# Revit family: Valve-Pressure_Relief-Cla_Val-55L_60-FNPT-SI--
name_source: partatom
category: Pipe Accessories
units: mm (PartAtom-declared; Revit-internal decimal feet)

## family parameters
Always vertical = Yes
Cut with Voids When Loaded = No
OmniClass Number = 23.65.55.00
OmniClass Title = Distribution of Supplied Liquids/Gases
Part Type = Valve - Breaks Into
Round Connector Dimension = Use Radius
Shared = No
Work Plane-Based = No

## types (1)
- ERROR_LOAD TYPE CATALOG
    Assembly Code = D2090900
    Bottom Plug Material = Metal - Cla-Val - Stainless Steel
    CV (liters per second) = 0.38
    Cap Height = 57 mm
    Cap Material = Plastic - Cla-Val - Red
    Cap Mount Height = 4 mm
    Cap Mount Radius = 11 mm
    Cap Radius = 10 mm
    Connection Axis to Lower Flange = 33 mm
    Connection Axis to Valve Bottom = 33 mm
    Connection Axis to Valve Top = 171 mm
    Connection Radius = 8 mm
    Connection Size = 15 mm
    Connection Type = Female Thread
    Connection to Connection = 62 mm
    Cover Bevel Radius = 6 mm
    Cover Radius = 17 mm
    Default Elevation = 0 mm
    Description = Pressure Relief Valve
    ENGworks Global = http://www.ENGworksGlobal.com
    Flow Configuration = In/Out
    K Coefficient = 3.717034
    K Coefficient Table = Globe Valve Threaded
    Lock Nut Circumscribe Length = 23 mm
    Lock Nut Height = 15 mm
    Loss Method = K Coefficient
    Lower Flange Height = 6 mm
    Manufacturer = Cla_Val
    Maximum Flow Rate = 1.6 L/s
    Maximum Flow Rate Value = 1.58
    Maximum Operating Temperature = 82 °C
    Maximum Working Pressure = 28 bar
    Minimum Flow Rate = 0.0 L/s
    Minimum Flow Rate Value = 0
    Minimum Operating Temperature = -18 °C
    Model = 55L-60
    Nut Union Circumscribe Length = 31 mm
    Overall Height = 219 mm
    Plug Mount Radius = 13 mm
    Pressure Gauge Port Outside Diameter = 10 mm
    Pressure Gauge Port Outside Radius = 5 mm
    Product Page URL = https://www.cla-val.com
    Series = Pressure Relief Valves
    Standards = UL Listed and FM Approved
    Threaded Female End Insertion Depth = 14 mm
    Threaded Female End Inside Diameter = 18 mm
    Threaded Female End Inside Radius = 9 mm
    Threaded Female End Outside Radius = 12 mm
    Tick Size = 36 mm
    URL = https://www.cla-val.com
    Unit Weight = 0 kgf
    Upper Flange Height = 6 mm
    Valve Body Diameter = 51 mm
    Valve Body Material = Metal - Cla-Val - Bronze
    Valve Body Radius = 25 mm
    Valve Flange Outside Diameter = 79 mm
    Valve Flange Outside Radius = 40 mm
    Valve Length = 89 mm
    Valve Main Body Plug Circumscribe Length = 18 mm
    Valve Plug Nut Height = 14 mm
    Valve Plug Nut Width = 15 mm
    Version = 1

## geometry (parser evidence)
native form markers: Sweep x3
no freeform markers — native parametric forms only
